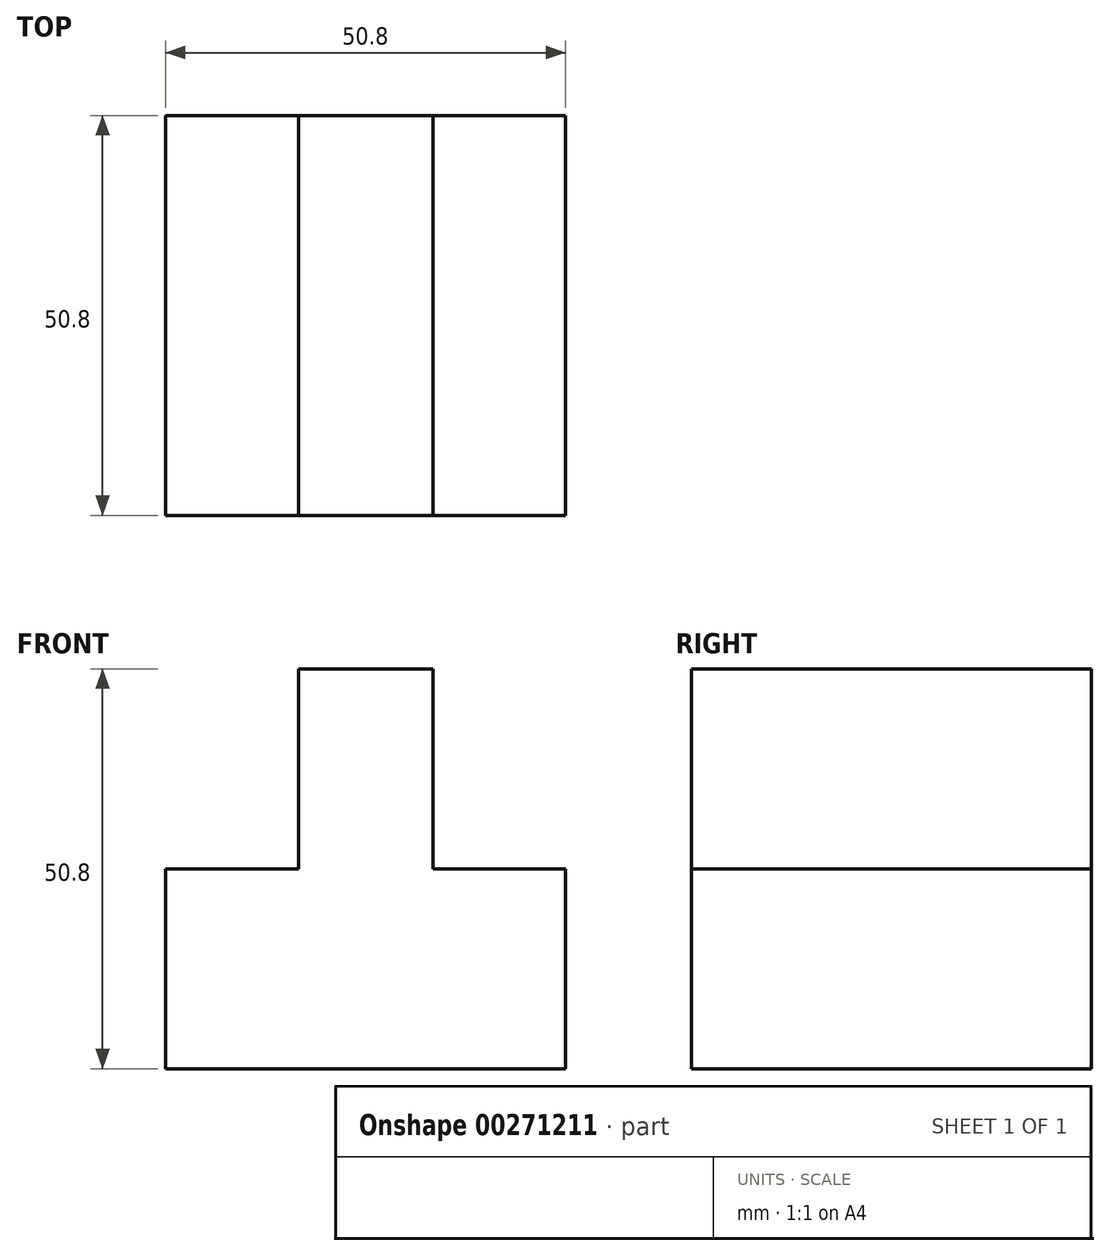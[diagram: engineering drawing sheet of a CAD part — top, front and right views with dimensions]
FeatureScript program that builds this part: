
annotation { "Feature Type Name" : "Feature", "Feature Type Description" : "" }
export const myFeature = defineFeature(function(context is Context, id is Id, definition is map)
    precondition{}
    {
        {
            var Q0;
            Q0=qCreatedBy(makeId("Front.planeOp"),FACE);
            var sketch = newSketch(context, id + "F0", { "sketchPlane" : qUnion([Q0])});
            skLineSegment(sketch, "E0.bottom", {"start": v(0, 0) * mm, "end": v(-50.8, 0) * mm});
            skLineSegment(sketch, "E0.top", {"start": v(0, 50.8) * mm, "end": v(-50.8, 50.8) * mm});
            skLineSegment(sketch, "E0.left", {"start": v(0, 0) * mm, "end": v(0, 50.8) * mm});
            skLineSegment(sketch, "E0.right", {"start": v(-50.8, 0) * mm, "end": v(-50.8, 50.8) * mm});
            skSolve(sketch);
        }
        {
            var Q0;
            Q0 = qSketchRegion(id + "F0", true);
            extrude(context, id + "F1", {"entities" : qUnion([Q0]), "depth" : 50.8 * mm});
        }
        {
            var Q0;
            Q0=makeQuery(id+"F1.opExtrude","CAP_FACE",FACE,{"disambiguationData":[OSD([sQuery(id+"F0.wireOp",EDGE,"E0.bottom"),sQuery(id+"F0.wireOp",EDGE,"E0.top"),sQuery(id+"F0.wireOp",EDGE,"E0.left"),sQuery(id+"F0.wireOp",EDGE,"E0.right")])],"isStart":false});
            var sketch = newSketch(context, id + "F2", { "sketchPlane" : qUnion([Q0])});
            skLineSegment(sketch, "E1", {"start": v(-50.8, 25.4) * mm, "end": v(-33.93, 25.4) * mm});
            skLineSegment(sketch, "E2", {"start": v(-33.93, 25.4) * mm, "end": v(-33.93, 50.8) * mm});
            skLineSegment(sketch, "E3", {"start": v(0, 25.4) * mm, "end": v(-16.84, 25.4) * mm});
            skPoint(sketch, "E3.endSnap0", {"position": v(0, 25.4) * mm});
            skLineSegment(sketch, "E4", {"start": v(-16.84, 25.4) * mm, "end": v(-16.84, 50.8) * mm});
            skLineSegment(sketch, "E5", {"start": v(-16.84, 50.8) * mm, "end": v(0, 50.8) * mm});
            skLineSegment(sketch, "E6", {"start": v(0, 50.8) * mm, "end": v(0, 25.4) * mm});
            skLineSegment(sketch, "E7", {"start": v(-33.93, 50.8) * mm, "end": v(-50.8, 50.8) * mm});
            skLineSegment(sketch, "E8", {"start": v(-50.8, 50.8) * mm, "end": v(-50.8, 25.4) * mm});
            skSolve(sketch);
        }
        {
            var Q0;
            Q0 = qSketchRegion(id + "F2", true);
            extrude(context, id + "F3", {"entities" : qUnion([Q0]), "operationType" : NewBodyOperationType.REMOVE, "oppositeDirection" : true, "depth" : 50.8 * mm});
        }
    });
